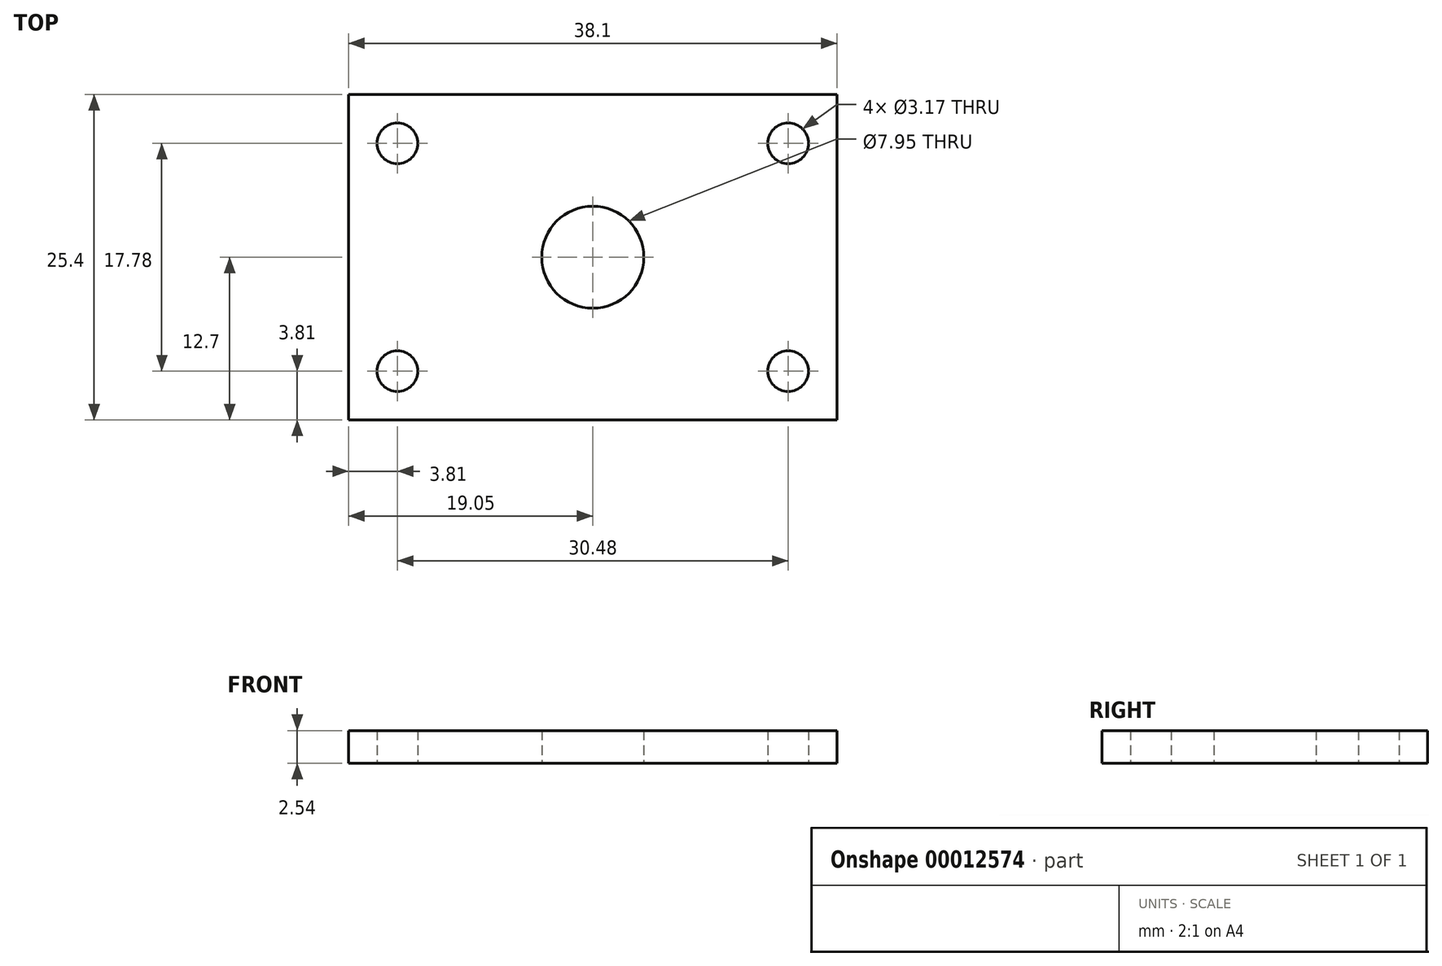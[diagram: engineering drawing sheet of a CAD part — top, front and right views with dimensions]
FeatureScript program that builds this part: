
annotation { "Feature Type Name" : "Feature", "Feature Type Description" : "" }
export const myFeature = defineFeature(function(context is Context, id is Id, definition is map)
    precondition{}
    {
        {
            var Q0;
            Q0=qCreatedBy(makeId("Top.planeOp"),FACE);
            var sketch = newSketch(context, id + "F0", { "sketchPlane" : qUnion([Q0])});
            skCircle(sketch, "E0", {"center": v(15.24, -8.9) * mm, "radius": 1.59 * mm});
            skCircle(sketch, "E1", {"center": v(15.24, 8.9) * mm, "radius": 1.59 * mm});
            skCircle(sketch, "E2", {"center": v(-15.24, 8.9) * mm, "radius": 1.59 * mm});
            skLineSegment(sketch, "E3.rect.right", {"start": v(15.24, 8.9) * mm, "end": v(15.24, -8.9) * mm, "construction": true});
            skLineSegment(sketch, "E3.rect.left", {"start": v(-15.24, 8.9) * mm, "end": v(-15.24, -8.9) * mm, "construction": true});
            skLineSegment(sketch, "E3.rect.top", {"start": v(-15.24, -8.9) * mm, "end": v(15.24, -8.9) * mm, "construction": true});
            skLineSegment(sketch, "E3.rect.bottom", {"start": v(-15.24, 8.9) * mm, "end": v(15.24, 8.9) * mm, "construction": true});
            skCircle(sketch, "E4", {"center": v(0, 0) * mm, "radius": 3.98 * mm});
            skCircle(sketch, "E5", {"center": v(-15.24, -8.9) * mm, "radius": 1.59 * mm});
            skLineSegment(sketch, "E6.rect.bottom", {"start": v(19.05, -12.7) * mm, "end": v(-19.05, -12.7) * mm});
            skLineSegment(sketch, "E6.rect.top", {"start": v(19.05, 12.7) * mm, "end": v(-19.05, 12.7) * mm});
            skLineSegment(sketch, "E6.rect.left", {"start": v(19.05, -12.7) * mm, "end": v(19.05, 12.7) * mm});
            skLineSegment(sketch, "E6.rect.right", {"start": v(-19.05, -12.7) * mm, "end": v(-19.05, 12.7) * mm});
            skSolve(sketch);
        }
        {
            var Q0;
            Q0 = qSketchRegion(id + "F0", true);
            extrude(context, id + "F1", {"entities" : qUnion([Q0]), "depth" : 2.54 * mm});
        }
    });
